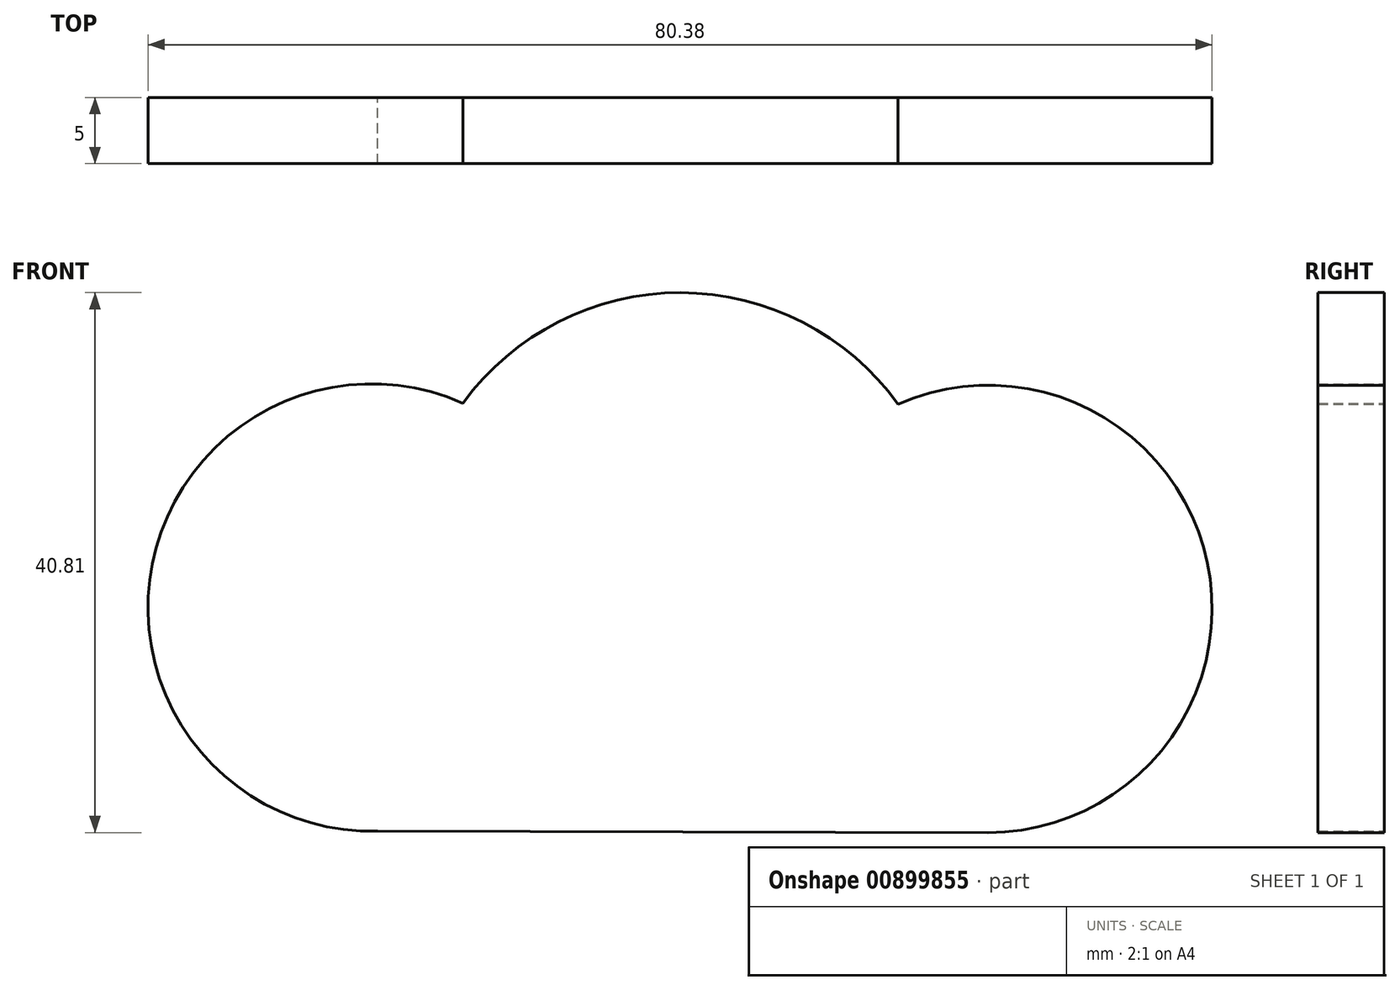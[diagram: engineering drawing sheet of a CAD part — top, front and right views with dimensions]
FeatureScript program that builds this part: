
annotation { "Feature Type Name" : "Feature", "Feature Type Description" : "" }
export const myFeature = defineFeature(function(context is Context, id is Id, definition is map)
    precondition{}
    {
        {
            var Q0;
            Q0=qCreatedBy(makeId("Front.planeOp"),FACE);
            var sketch = newSketch(context, id + "F0", { "sketchPlane" : qUnion([Q0])});
            skArc(sketch, "E0", {"start": v(16.46, 11.86) * mm, "mid": v(0.04, 20.29) * mm, "end": v(-16.4, 11.93) * mm});
            skArc(sketch, "E1", {"start": v(-16.4, 11.93) * mm, "mid": v(-40.02, -1.03) * mm, "end": v(-21.2, -20.29) * mm});
            skPoint(sketch, "E1.first.point", {"position": v(-21.2, -20.29) * mm});
            skPoint(sketch, "E1.second.point", {"position": v(-18.24, 12.62) * mm});
            skPoint(sketch, "E1.second.point.positionSnap0", {"position": v(-18.24, -20.29) * mm});
            skPoint(sketch, "E1.third.point", {"position": v(-36.17, 7.44) * mm});
            skArc(sketch, "E2", {"start": v(23.24, -20.52) * mm, "mid": v(39.82, -0.15) * mm, "end": v(16.46, 11.86) * mm});
            skPoint(sketch, "E2.first.point", {"position": v(26.06, -20.29) * mm});
            skPoint(sketch, "E2.second.point", {"position": v(20.49, -20.29) * mm});
            skPoint(sketch, "E2.third.point", {"position": v(20.26, 13.02) * mm});
            skLineSegment(sketch, "E3", {"start": v(-22.87, -20.41) * mm, "end": v(23.24, -20.52) * mm});
            skLineSegment(sketch, "E4", {"start": v(-40.02, -1.03) * mm, "end": v(39.98, -1.03) * mm});
            skSolve(sketch);
        }
        {
            var Q0;
            {var subQ0=sQuery(id+"F0.wireOp",EDGE,"E3");Q0=makeQuery(id+"F0.imprint","IMPRINT",FACE,{"disambiguationData":[TD([[makeQuery(id+"F0.imprint","IMPRINT",EDGE,{"derivedFrom":subQ0}),1.0]])]});}
            var Q1;
            {var subQ0=sQuery(id+"F0.wireOp",EDGE,"E0");Q1=makeQuery(id+"F0.imprint","IMPRINT",FACE,{"disambiguationData":[TD([[makeQuery(id+"F0.imprint","IMPRINT",EDGE,{"derivedFrom":subQ0}),1.0]])]});}
            extrude(context, id + "F1", {"entities" : qUnion([Q0, Q1]), "depth" : 5 * mm, "offsetDistance" : 25 * mm});
        }
    });
